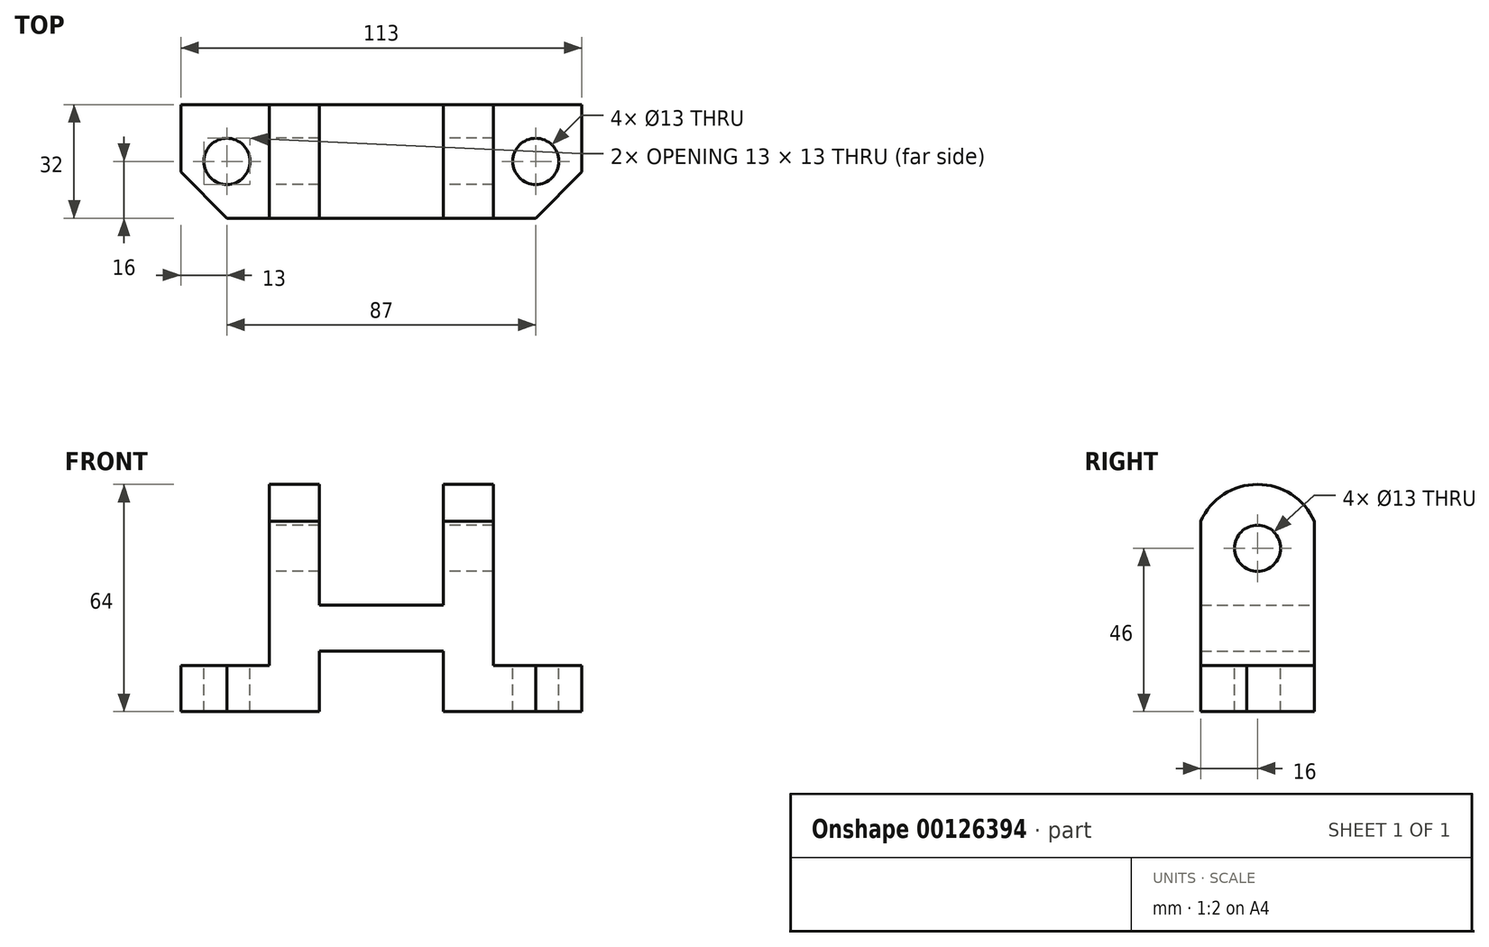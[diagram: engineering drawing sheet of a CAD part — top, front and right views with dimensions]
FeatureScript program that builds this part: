
annotation { "Feature Type Name" : "Feature", "Feature Type Description" : "" }
export const myFeature = defineFeature(function(context is Context, id is Id, definition is map)
    precondition{}
    {
        {
            var Q0;
            Q0=qCreatedBy(makeId("Right.planeOp"),FACE);
            var sketch = newSketch(context, id + "F0", { "sketchPlane" : qUnion([Q0])});
            skLineSegment(sketch, "E0.bottom", {"start": v(16, 0) * mm, "end": v(-16, 0) * mm});
            skLineSegment(sketch, "E0.top", {"start": v(16, 64) * mm, "end": v(-16, 64) * mm});
            skLineSegment(sketch, "E0.left", {"start": v(16, 0) * mm, "end": v(16, 64) * mm});
            skLineSegment(sketch, "E0.right", {"start": v(-16, 0) * mm, "end": v(-16, 64) * mm});
            skCircle(sketch, "E1", {"center": v(0, 46) * mm, "radius": 6.5 * mm});
            skArc(sketch, "E2", {"start": v(16, 53.59) * mm, "mid": v(0, 64) * mm, "end": v(-16, 53.59) * mm});
            skPoint(sketch, "E3", {"position": v(0, 64) * mm});
            skSolve(sketch);
        }
        {
            var Q0;
            {var subQ1=sQuery(id+"F0.wireOp",EDGE,"E0.bottom");Q0=makeQuery(id+"F0.imprint","IMPRINT",FACE,{"disambiguationData":[TD([[makeQuery(id+"F0.imprint","IMPRINT",EDGE,{"derivedFrom":subQ1}),-1.0]])]});}
            extrude(context, id + "F1", {"entities" : qUnion([Q0]), "endBound" : BoundingType.SYMMETRIC, "depth" : 113 * mm});
        }
        {
            var Q0;
            Q0=makeQuery(id+"F1.opExtrude","SWEPT_FACE",FACE,{"disambiguationData":[OSD([sQuery(id+"F0.wireOp",EDGE,"E0.left")])]});
            var sketch = newSketch(context, id + "F2", { "sketchPlane" : qUnion([Q0])});
            skLineSegment(sketch, "E4.bottom", {"start": v(56.5, 13) * mm, "end": v(31.5, 13) * mm});
            skLineSegment(sketch, "E4.top", {"start": v(56.5, 64) * mm, "end": v(31.5, 64) * mm});
            skLineSegment(sketch, "E4.left", {"start": v(56.5, 13) * mm, "end": v(56.5, 64) * mm});
            skLineSegment(sketch, "E4.right", {"start": v(31.5, 13) * mm, "end": v(31.5, 64) * mm});
            skLineSegment(sketch, "E5.bottom", {"start": v(-56.5, 13) * mm, "end": v(-31.5, 13) * mm});
            skLineSegment(sketch, "E5.top", {"start": v(-56.5, 64) * mm, "end": v(-31.5, 64) * mm});
            skLineSegment(sketch, "E5.left", {"start": v(-56.5, 13) * mm, "end": v(-56.5, 64) * mm});
            skLineSegment(sketch, "E5.right", {"start": v(-31.5, 13) * mm, "end": v(-31.5, 64) * mm});
            skLineSegment(sketch, "E6.bottom", {"start": v(-17.5, 0) * mm, "end": v(17.5, 0) * mm});
            skLineSegment(sketch, "E6.top", {"start": v(-17.5, 17) * mm, "end": v(17.5, 17) * mm});
            skLineSegment(sketch, "E6.left", {"start": v(-17.5, 0) * mm, "end": v(-17.5, 17) * mm});
            skLineSegment(sketch, "E6.right", {"start": v(17.5, 0) * mm, "end": v(17.5, 17) * mm});
            skLineSegment(sketch, "E7.bottom", {"start": v(-17.5, 30) * mm, "end": v(17.5, 30) * mm});
            skLineSegment(sketch, "E7.top", {"start": v(-17.5, 64) * mm, "end": v(17.5, 64) * mm});
            skLineSegment(sketch, "E7.left", {"start": v(-17.5, 30) * mm, "end": v(-17.5, 64) * mm});
            skLineSegment(sketch, "E7.right", {"start": v(17.5, 30) * mm, "end": v(17.5, 64) * mm});
            skSolve(sketch);
        }
        {
            var Q0;
            Q0 = qSketchRegion(id + "F2", true);
            extrude(context, id + "F3", {"entities" : qUnion([Q0]), "operationType" : NewBodyOperationType.REMOVE, "endBound" : BoundingType.THROUGH_ALL, "oppositeDirection" : true, "depth" : 25 * mm});
        }
        {
            var Q0;
            Q0=makeQuery(id+"F3.boolean.opBoolean","COPY",FACE,{"derivedFrom":makeQuery(id+"F3.opExtrude","SWEPT_FACE",FACE,{"disambiguationData":[OSD([sQuery(id+"F2.wireOp",EDGE,"E4.bottom")])]})});
            var sketch = newSketch(context, id + "F4", { "sketchPlane" : qUnion([Q0])});
            skCircle(sketch, "E8", {"center": v(-43.5, 0) * mm, "radius": 6.5 * mm});
            skLineSegment(sketch, "E9", {"start": v(-56.5, -16) * mm, "end": v(-43.5, -16) * mm});
            skLineSegment(sketch, "E10", {"start": v(-43.5, -16) * mm, "end": v(-56.5, -3) * mm});
            skLineSegment(sketch, "E11", {"start": v(-56.5, -3) * mm, "end": v(-56.5, -16) * mm});
            skSolve(sketch);
        }
        {
            var Q0;
            Q0 = qSketchRegion(id + "F4", true);
            extrude(context, id + "F5", {"entities" : qUnion([Q0]), "operationType" : NewBodyOperationType.REMOVE, "endBound" : BoundingType.THROUGH_ALL, "oppositeDirection" : true, "depth" : 25 * mm});
        }
        {
            var Q0;
            Q0=makeQuery(id+"F3.boolean.opBoolean","COPY",FACE,{"derivedFrom":makeQuery(id+"F3.opExtrude","SWEPT_FACE",FACE,{"disambiguationData":[OSD([sQuery(id+"F2.wireOp",EDGE,"E5.bottom")])]})});
            var sketch = newSketch(context, id + "F6", { "sketchPlane" : qUnion([Q0])});
            skCircle(sketch, "E12", {"center": v(43.5, 0) * mm, "radius": 6.5 * mm});
            skLineSegment(sketch, "E13", {"start": v(43.5, -16) * mm, "end": v(56.5, -16) * mm});
            skLineSegment(sketch, "E14", {"start": v(56.5, -16) * mm, "end": v(56.5, -3) * mm});
            skLineSegment(sketch, "E15", {"start": v(56.5, -3) * mm, "end": v(43.5, -16) * mm});
            skSolve(sketch);
        }
        {
            var Q0;
            Q0 = qSketchRegion(id + "F6", true);
            extrude(context, id + "F7", {"entities" : qUnion([Q0]), "operationType" : NewBodyOperationType.REMOVE, "endBound" : BoundingType.THROUGH_ALL, "oppositeDirection" : true, "depth" : 25 * mm});
        }
    });
